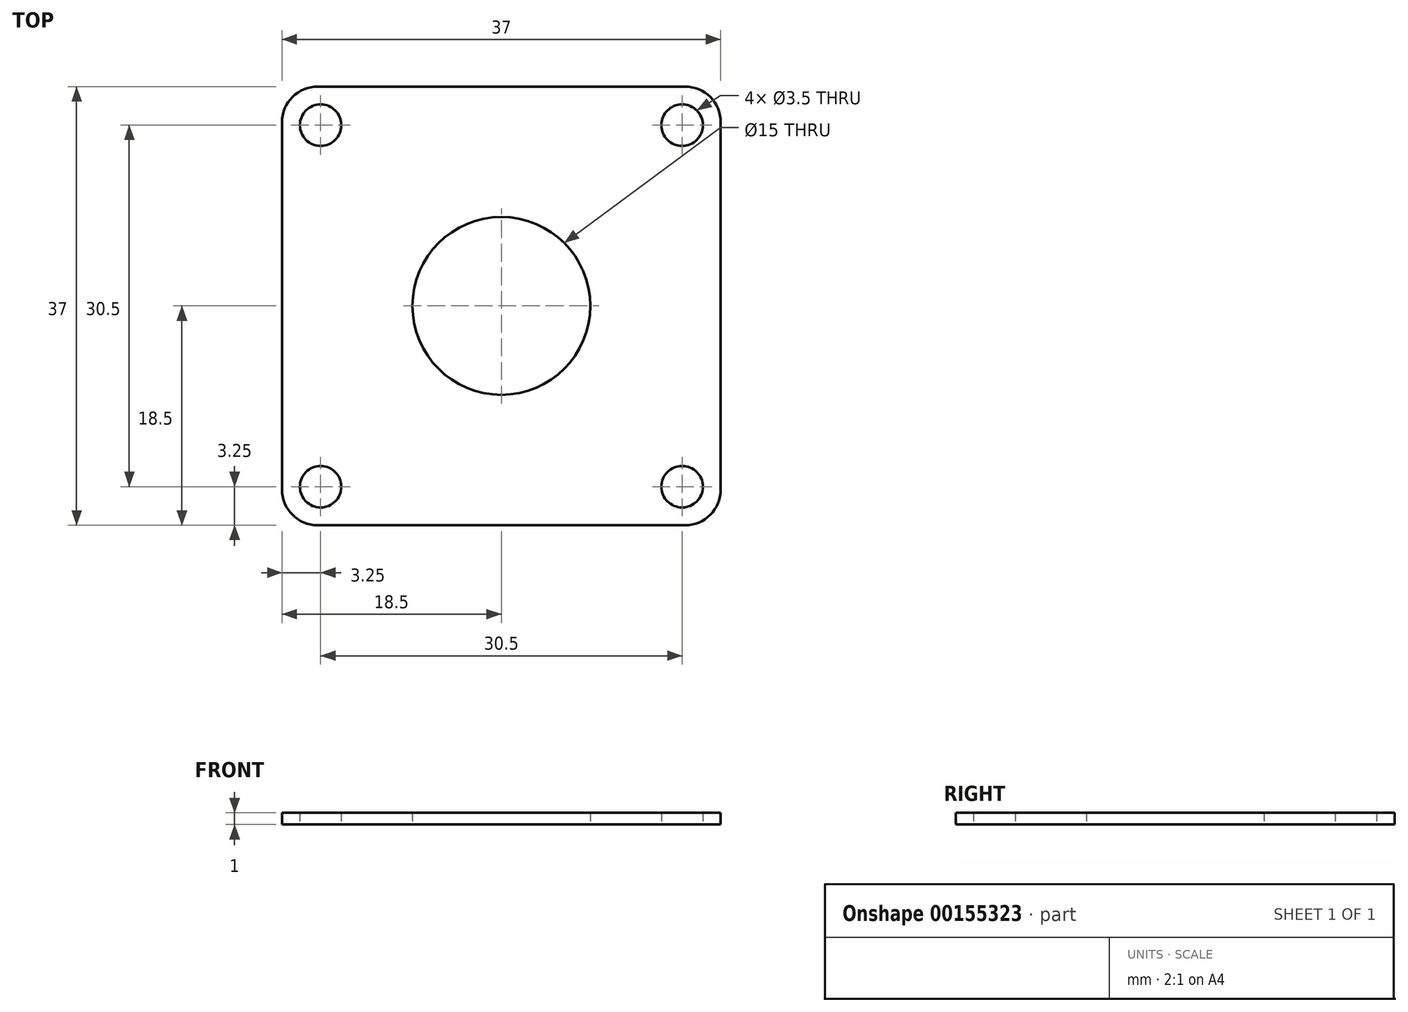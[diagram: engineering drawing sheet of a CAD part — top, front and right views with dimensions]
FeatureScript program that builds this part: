
annotation { "Feature Type Name" : "Feature", "Feature Type Description" : "" }
export const myFeature = defineFeature(function(context is Context, id is Id, definition is map)
    precondition{}
    {
        {
            var Q0;
            Q0=qCreatedBy(makeId("Top.planeOp"),FACE);
            var sketch = newSketch(context, id + "F0", { "sketchPlane" : qUnion([Q0])});
            skCircle(sketch, "E0", {"center": v(-15.25, 15.25) * mm, "radius": 1.75 * mm});
            skCircle(sketch, "E1", {"center": v(15.25, 15.25) * mm, "radius": 1.75 * mm});
            skCircle(sketch, "E2", {"center": v(15.25, -15.25) * mm, "radius": 1.75 * mm});
            skCircle(sketch, "E3", {"center": v(-15.25, -15.25) * mm, "radius": 1.75 * mm});
            skLineSegment(sketch, "E4.bottom", {"start": v(-18.5, 18.5) * mm, "end": v(18.5, 18.5) * mm});
            skLineSegment(sketch, "E4.top", {"start": v(-18.5, -18.5) * mm, "end": v(18.5, -18.5) * mm});
            skLineSegment(sketch, "E4.left", {"start": v(-18.5, 18.5) * mm, "end": v(-18.5, -18.5) * mm});
            skLineSegment(sketch, "E4.right", {"start": v(18.5, 18.5) * mm, "end": v(18.5, -18.5) * mm});
            skCircle(sketch, "E5", {"center": v(0, 0) * mm, "radius": 7.5 * mm});
            skSolve(sketch);
        }
        {
            var Q0;
            Q0 = qSketchRegion(id + "F0", true);
            extrude(context, id + "F1", {"entities" : qUnion([Q0]), "depth" : 1 * mm});
        }
        {
            var Q0;
            Q0=makeQuery(id+"F1.opExtrude","SWEPT_EDGE",EDGE,{"disambiguationData":[OSD([sQuery(id+"F0.wireOp",EDGE,"E4.top"),sQuery(id+"F0.wireOp",EDGE,"E4.left")])]});
            var Q1;
            Q1=makeQuery(id+"F1.opExtrude","SWEPT_EDGE",EDGE,{"disambiguationData":[OSD([sQuery(id+"F0.wireOp",EDGE,"E4.top"),sQuery(id+"F0.wireOp",EDGE,"E4.right")])]});
            var Q2;
            Q2=makeQuery(id+"F1.opExtrude","SWEPT_EDGE",EDGE,{"disambiguationData":[OSD([sQuery(id+"F0.wireOp",EDGE,"E4.bottom"),sQuery(id+"F0.wireOp",EDGE,"E4.right")])]});
            var Q3;
            Q3=makeQuery(id+"F1.opExtrude","SWEPT_EDGE",EDGE,{"disambiguationData":[OSD([sQuery(id+"F0.wireOp",EDGE,"E4.bottom"),sQuery(id+"F0.wireOp",EDGE,"E4.left")])]});
            fillet(context, id + "F2", {"entities" : qUnion([Q0, Q1, Q2, Q3]), "radius" : 3 * mm, "tangentPropagation" : true, "allowEdgeOverflow" : false});
        }
    });
